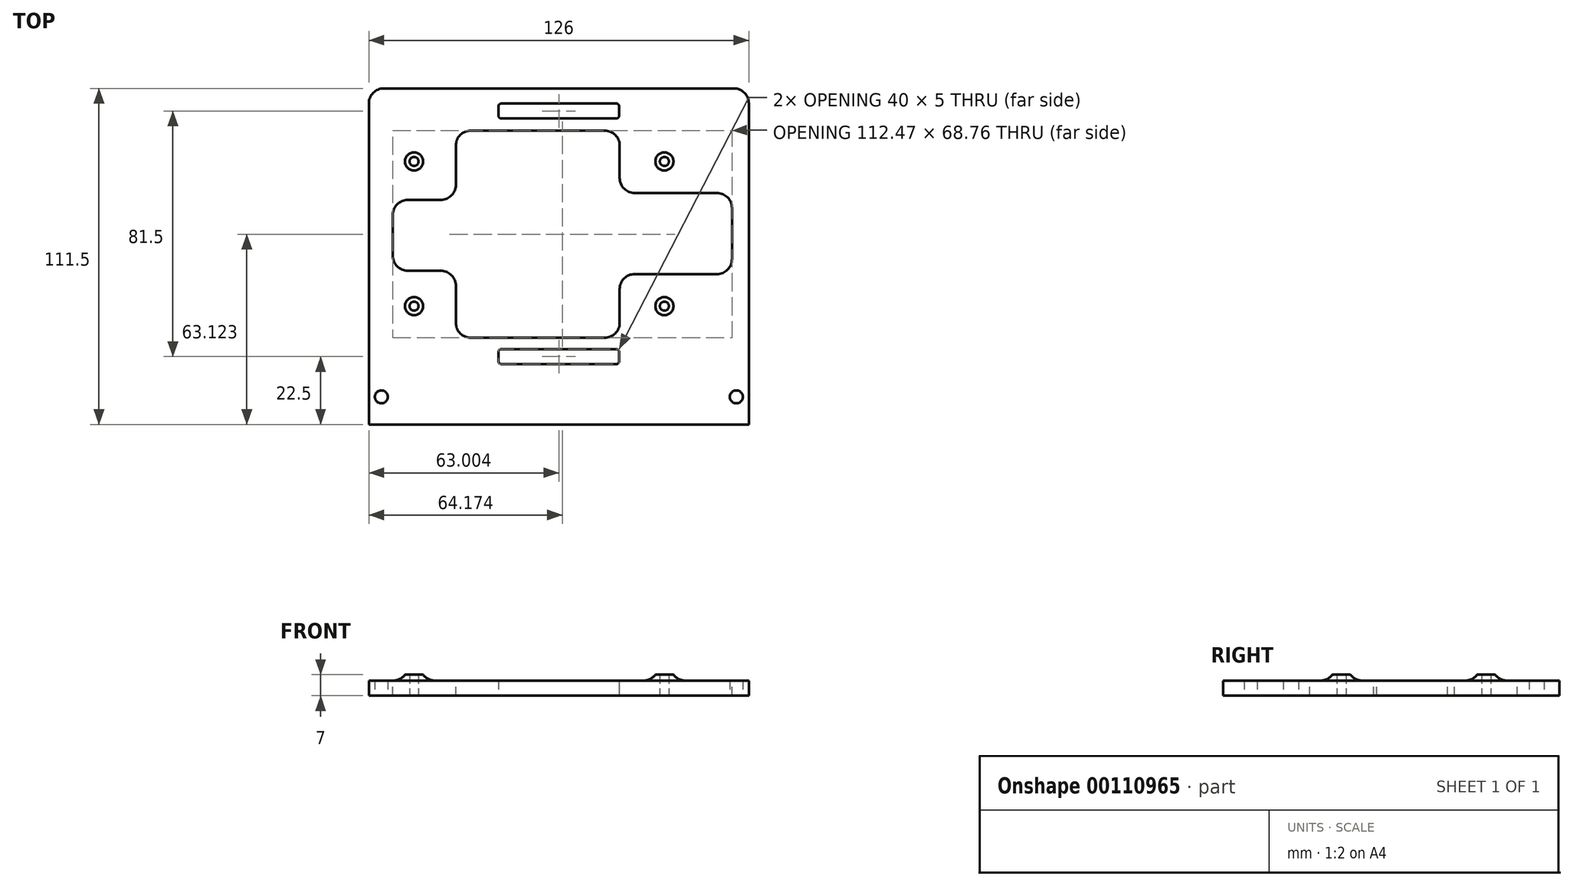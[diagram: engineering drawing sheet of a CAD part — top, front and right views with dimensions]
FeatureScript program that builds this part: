
annotation { "Feature Type Name" : "Feature", "Feature Type Description" : "" }
export const myFeature = defineFeature(function(context is Context, id is Id, definition is map)
    precondition{}
    {
        {
            var Q0;
            Q0=qCreatedBy(makeId("Top.planeOp"),FACE);
            var sketch = newSketch(context, id + "F0", { "sketchPlane" : qUnion([Q0])});
            skLineSegment(sketch, "E0.bottom", {"start": v(-49.76, 0) * mm, "end": v(76.24, 0) * mm});
            skLineSegment(sketch, "E0.top", {"start": v(-49.76, 111.5) * mm, "end": v(76.24, 111.5) * mm});
            skLineSegment(sketch, "E0.left", {"start": v(-49.76, 0) * mm, "end": v(-49.76, 111.5) * mm});
            skLineSegment(sketch, "E0.right", {"start": v(76.24, 0) * mm, "end": v(76.24, 111.5) * mm});
            skLineSegment(sketch, "E1.top", {"start": v(-49.76, 20) * mm, "end": v(76.24, 20) * mm});
            skLineSegment(sketch, "E1.left", {"start": v(-49.76, 0) * mm, "end": v(-49.76, 20) * mm});
            skLineSegment(sketch, "E1.right", {"start": v(76.24, 0) * mm, "end": v(76.24, 20) * mm});
            skLineSegment(sketch, "E2.bottom", {"start": v(-6.76, 20) * mm, "end": v(33.24, 20) * mm});
            skLineSegment(sketch, "E2.top", {"start": v(-6.76, 25) * mm, "end": v(33.24, 25) * mm});
            skLineSegment(sketch, "E2.left", {"start": v(-6.76, 20) * mm, "end": v(-6.76, 25) * mm});
            skLineSegment(sketch, "E2.right", {"start": v(33.24, 20) * mm, "end": v(33.24, 25) * mm});
            skPoint(sketch, "E3", {"position": v(13.24, 111.5) * mm});
            skPoint(sketch, "E4", {"position": v(13.24, 25) * mm});
            skLineSegment(sketch, "E5.top", {"start": v(-49.76, 106.5) * mm, "end": v(76.24, 106.5) * mm});
            skLineSegment(sketch, "E5.left", {"start": v(-49.76, 111.5) * mm, "end": v(-49.76, 106.5) * mm});
            skLineSegment(sketch, "E5.right", {"start": v(76.24, 111.5) * mm, "end": v(76.24, 106.5) * mm});
            skCircle(sketch, "E6", {"center": v(13.24, 63.25) * mm, "radius": 5 * mm});
            skCircle(sketch, "E7", {"center": v(23.24, 53.25) * mm, "radius": 1.5 * mm});
            skCircle(sketch, "E8", {"center": v(3.24, 53.25) * mm, "radius": 1.5 * mm});
            skCircle(sketch, "E9", {"center": v(3.24, 73.25) * mm, "radius": 1.5 * mm});
            skCircle(sketch, "E10", {"center": v(23.24, 73.25) * mm, "radius": 1.5 * mm});
            skLineSegment(sketch, "E11", {"start": v(23.24, 73.25) * mm, "end": v(23.24, 53.25) * mm, "construction": true});
            skLineSegment(sketch, "E12", {"start": v(3.24, 73.25) * mm, "end": v(23.24, 73.25) * mm, "construction": true});
            skPoint(sketch, "E13", {"position": v(23.24, 63.25) * mm});
            skPoint(sketch, "E14", {"position": v(13.24, 73.25) * mm});
            skLineSegment(sketch, "E15", {"start": v(23.24, 73.25) * mm, "end": v(23.24, 106.5) * mm, "construction": true});
            skLineSegment(sketch, "E16", {"start": v(23.24, 53.25) * mm, "end": v(23.24, 20) * mm, "construction": true});
            skCircle(sketch, "E17", {"center": v(-34.76, 87.25) * mm, "radius": 3 * mm});
            skCircle(sketch, "E18", {"center": v(-34.76, 39.25) * mm, "radius": 3 * mm});
            skCircle(sketch, "E19", {"center": v(48.24, 87.25) * mm, "radius": 3 * mm});
            skCircle(sketch, "E20", {"center": v(48.24, 39.25) * mm, "radius": 3 * mm});
            skLineSegment(sketch, "E21", {"start": v(-34.76, 87.25) * mm, "end": v(48.24, 87.25) * mm, "construction": true});
            skLineSegment(sketch, "E22", {"start": v(48.24, 87.25) * mm, "end": v(48.24, 39.25) * mm, "construction": true});
            skCircle(sketch, "E23", {"center": v(-34.76, 87.25) * mm, "radius": 1.5 * mm});
            skCircle(sketch, "E24", {"center": v(-34.76, 39.25) * mm, "radius": 1.5 * mm});
            skCircle(sketch, "E25", {"center": v(48.24, 39.25) * mm, "radius": 1.5 * mm});
            skCircle(sketch, "E26", {"center": v(48.24, 87.25) * mm, "radius": 1.5 * mm});
            skLineSegment(sketch, "E27", {"start": v(48.24, 39.25) * mm, "end": v(48.24, 20) * mm, "construction": true});
            skLineSegment(sketch, "E28", {"start": v(48.24, 87.25) * mm, "end": v(48.24, 106.5) * mm, "construction": true});
            skCircle(sketch, "E29", {"center": v(-45.6, 9.15) * mm, "radius": 2.15 * mm});
            skCircle(sketch, "E30", {"center": v(72.1, 9.15) * mm, "radius": 2.15 * mm});
            skLineSegment(sketch, "E31.bottom", {"start": v(-6.76, 106.5) * mm, "end": v(33.24, 106.5) * mm});
            skLineSegment(sketch, "E31.top", {"start": v(-6.76, 101.5) * mm, "end": v(33.24, 101.5) * mm});
            skLineSegment(sketch, "E31.left", {"start": v(-6.76, 106.5) * mm, "end": v(-6.76, 101.5) * mm});
            skLineSegment(sketch, "E31.right", {"start": v(33.24, 106.5) * mm, "end": v(33.24, 101.5) * mm});
            skSolve(sketch);
        }
        {
            var Q0;
            Q0=qSketchRegion(id+"F0",true);
            var Q1;
            Q1=makeQuery(id+"F0.imprint","IMPRINT",FACE,{"disambiguationData":[TD([[makeQuery(id+"F0.imprint","IMPRINT",EDGE,{"derivedFrom":sQuery(id+"F0.wireOp",EDGE,"E18")}),1.0]])]});
            var Q2;
            Q2=makeQuery(id+"F0.imprint","IMPRINT",FACE,{"disambiguationData":[TD([[makeQuery(id+"F0.imprint","IMPRINT",EDGE,{"derivedFrom":sQuery(id+"F0.wireOp",EDGE,"E17")}),1.0]])]});
            var Q3;
            Q3=makeQuery(id+"F0.imprint","IMPRINT",FACE,{"disambiguationData":[TD([[makeQuery(id+"F0.imprint","IMPRINT",EDGE,{"derivedFrom":sQuery(id+"F0.wireOp",EDGE,"E20")}),1.0]])]});
            var Q4;
            Q4=makeQuery(id+"F0.imprint","IMPRINT",FACE,{"disambiguationData":[TD([[makeQuery(id+"F0.imprint","IMPRINT",EDGE,{"derivedFrom":sQuery(id+"F0.wireOp",EDGE,"E19")}),1.0]])]});
            var Q5;
            Q5=makeQuery(id+"F0.imprint","IMPRINT",FACE,{"disambiguationData":[TD([[makeQuery(id+"F0.imprint","IMPRINT",EDGE,{"derivedFrom":sQuery(id+"F0.wireOp",EDGE,"E6")}),1.0]])]});
            var Q6;
            Q6=makeQuery(id+"F0.imprint","IMPRINT",FACE,{"disambiguationData":[TD([[makeQuery(id+"F0.imprint","IMPRINT",EDGE,{"derivedFrom":sQuery(id+"F0.wireOp",EDGE,"E9")}),1.0]])]});
            var Q7;
            Q7=makeQuery(id+"F0.imprint","IMPRINT",FACE,{"disambiguationData":[TD([[makeQuery(id+"F0.imprint","IMPRINT",EDGE,{"derivedFrom":sQuery(id+"F0.wireOp",EDGE,"E8")}),1.0]])]});
            var Q8;
            Q8=makeQuery(id+"F0.imprint","IMPRINT",FACE,{"disambiguationData":[TD([[makeQuery(id+"F0.imprint","IMPRINT",EDGE,{"derivedFrom":sQuery(id+"F0.wireOp",EDGE,"E7")}),1.0]])]});
            var Q9;
            Q9=makeQuery(id+"F0.imprint","IMPRINT",FACE,{"disambiguationData":[TD([[makeQuery(id+"F0.imprint","IMPRINT",EDGE,{"derivedFrom":sQuery(id+"F0.wireOp",EDGE,"E10")}),1.0]])]});
            extrude(context, id + "F1", {"entities" : qUnion([Q0, Q1, Q2, Q3, Q4, Q5, Q6, Q7, Q8, Q9]), "depth" : 5 * mm});
        }
        {
            var Q0;
            Q0=makeQuery(id+"F1.opExtrude","SWEPT_EDGE",EDGE,{"disambiguationData":[OSD([sQuery(id+"F0.wireOp",EDGE,"E2.top"),sQuery(id+"F0.wireOp",EDGE,"E2.left")])]});
            var Q1;
            Q1=makeQuery(id+"F1.opExtrude","SWEPT_EDGE",EDGE,{"disambiguationData":[OSD([sQuery(id+"F0.wireOp",EDGE,"E2.top"),sQuery(id+"F0.wireOp",EDGE,"E2.right")])]});
            var Q2;
            Q2=makeQuery(id+"F1.opExtrude","SWEPT_EDGE",EDGE,{"disambiguationData":[OSD([sQuery(id+"F0.wireOp",EDGE,"E1.top"),sQuery(id+"F0.wireOp",EDGE,"E2.bottom"),sQuery(id+"F0.wireOp",EDGE,"E2.left")])]});
            var Q3;
            Q3=makeQuery(id+"F1.opExtrude","SWEPT_EDGE",EDGE,{"disambiguationData":[OSD([sQuery(id+"F0.wireOp",EDGE,"E1.top"),sQuery(id+"F0.wireOp",EDGE,"E2.bottom"),sQuery(id+"F0.wireOp",EDGE,"E2.right")])]});
            var Q4;
            Q4=makeQuery(id+"F1.opExtrude","SWEPT_EDGE",EDGE,{"disambiguationData":[OSD([sQuery(id+"F0.wireOp",EDGE,"E31.top"),sQuery(id+"F0.wireOp",EDGE,"E31.left")])]});
            var Q5;
            Q5=makeQuery(id+"F1.opExtrude","SWEPT_EDGE",EDGE,{"disambiguationData":[OSD([sQuery(id+"F0.wireOp",EDGE,"E5.top"),sQuery(id+"F0.wireOp",EDGE,"E31.bottom"),sQuery(id+"F0.wireOp",EDGE,"E31.left")])]});
            var Q6;
            Q6=makeQuery(id+"F1.opExtrude","SWEPT_EDGE",EDGE,{"disambiguationData":[OSD([sQuery(id+"F0.wireOp",EDGE,"E5.top"),sQuery(id+"F0.wireOp",EDGE,"E31.bottom"),sQuery(id+"F0.wireOp",EDGE,"E31.right")])]});
            var Q7;
            Q7=makeQuery(id+"F1.opExtrude","SWEPT_EDGE",EDGE,{"disambiguationData":[OSD([sQuery(id+"F0.wireOp",EDGE,"E31.top"),sQuery(id+"F0.wireOp",EDGE,"E31.right")])]});
            fillet(context, id + "F2", {"entities" : qUnion([Q0, Q1, Q2, Q3, Q4, Q5, Q6, Q7]), "radius" : 1 * mm, "tangentPropagation" : true, "allowEdgeOverflow" : false});
        }
        {
            var Q0;
            {var subQ0=sQuery(id+"F0.wireOp",EDGE,"E5.left");var subQ1=sQuery(id+"F0.wireOp",EDGE,"E0.top");Q0=makeQuery(id+"FNY0aRx3992dt0J_1.boolean.opBoolean","MERGE",EDGE,{"derivedFrom":[makeQuery(id+"F1.opExtrude","SWEPT_EDGE",EDGE,{"disambiguationData":[OSD([subQ1,subQ0])]}),makeQuery(id+"FNY0aRx3992dt0J_1.opExtrude","SWEPT_EDGE",EDGE,{"disambiguationData":[OSD([subQ1,subQ0])]})]});}
            var Q1;
            {var subQ0=sQuery(id+"F0.wireOp",EDGE,"E1.left");var subQ1=sQuery(id+"F0.wireOp",EDGE,"E0.bottom");Q1=makeQuery(id+"FNY0aRx3992dt0J_1.boolean.opBoolean","MERGE",EDGE,{"derivedFrom":[makeQuery(id+"F1.opExtrude","SWEPT_EDGE",EDGE,{"disambiguationData":[OSD([subQ1,subQ0])]}),makeQuery(id+"FNY0aRx3992dt0J_1.opExtrude","SWEPT_EDGE",EDGE,{"disambiguationData":[OSD([subQ1,subQ0])]})]});}
            var Q2;
            Q2=makeQuery(id+"F1.opExtrude","SWEPT_EDGE",EDGE,{"disambiguationData":[OSD([sQuery(id+"F0.wireOp",EDGE,"E0.bottom"),sQuery(id+"F0.wireOp",EDGE,"E1.left")])]});
            var Q3;
            Q3=makeQuery(id+"F1.opExtrude","SWEPT_EDGE",EDGE,{"disambiguationData":[OSD([sQuery(id+"F0.wireOp",EDGE,"E0.bottom"),sQuery(id+"F0.wireOp",EDGE,"E1.right")])]});
            var Q4;
            Q4=makeQuery(id+"F1.opExtrude","SWEPT_EDGE",EDGE,{"disambiguationData":[OSD([sQuery(id+"F0.wireOp",EDGE,"E0.top"),sQuery(id+"F0.wireOp",EDGE,"E5.right")])]});
            fillet(context, id + "F3", {"entities" : qUnion([Q0, Q1, Q2, Q3, Q4]), "radius" : 5 * mm, "tangentPropagation" : true, "allowEdgeOverflow" : false});
        }
        {
            var Q0;
            Q0=makeQuery(id+"F0.imprint","IMPRINT",FACE,{"disambiguationData":[TD([[makeQuery(id+"F0.imprint","IMPRINT",EDGE,{"derivedFrom":sQuery(id+"F0.wireOp",EDGE,"E17")}),1.0]])]});
            var Q1;
            Q1=makeQuery(id+"F0.imprint","IMPRINT",FACE,{"disambiguationData":[TD([[makeQuery(id+"F0.imprint","IMPRINT",EDGE,{"derivedFrom":sQuery(id+"F0.wireOp",EDGE,"E18")}),1.0]])]});
            var Q2;
            Q2=makeQuery(id+"F0.imprint","IMPRINT",FACE,{"disambiguationData":[TD([[makeQuery(id+"F0.imprint","IMPRINT",EDGE,{"derivedFrom":sQuery(id+"F0.wireOp",EDGE,"E19")}),1.0]])]});
            var Q3;
            Q3=makeQuery(id+"F0.imprint","IMPRINT",FACE,{"disambiguationData":[TD([[makeQuery(id+"F0.imprint","IMPRINT",EDGE,{"derivedFrom":sQuery(id+"F0.wireOp",EDGE,"E20")}),1.0]])]});
            extrude(context, id + "F4", {"entities" : qUnion([Q0, Q1, Q2, Q3]), "operationType" : NewBodyOperationType.ADD, "depth" : 7 * mm});
        }
        {
            var Q0;
            Q0=makeQuery(id+"F4.boolean.opBoolean","INTERSECT",EDGE,{"derivedFrom":[makeQuery(id+"F1.opExtrude","CAP_FACE",FACE,{"disambiguationData":[OSD([sQuery(id+"F0.wireOp",EDGE,"E0.left"),sQuery(id+"F0.wireOp",EDGE,"E0.right"),sQuery(id+"F0.wireOp",EDGE,"E0.bottom"),sQuery(id+"F0.wireOp",EDGE,"E1.left"),sQuery(id+"F0.wireOp",EDGE,"E1.right"),sQuery(id+"F0.wireOp",EDGE,"E2.bottom"),sQuery(id+"F0.wireOp",EDGE,"E2.top"),sQuery(id+"F0.wireOp",EDGE,"E2.left"),sQuery(id+"F0.wireOp",EDGE,"E2.right"),sQuery(id+"F0.wireOp",EDGE,"E0.top"),sQuery(id+"F0.wireOp",EDGE,"E5.left"),sQuery(id+"F0.wireOp",EDGE,"E5.right"),sQuery(id+"F0.wireOp",EDGE,"E6"),sQuery(id+"F0.wireOp",EDGE,"E7"),sQuery(id+"F0.wireOp",EDGE,"E8"),sQuery(id+"F0.wireOp",EDGE,"E9"),sQuery(id+"F0.wireOp",EDGE,"E10")])],"isStart":false}),makeQuery(id+"F4.opExtrude","SWEPT_FACE",FACE,{"disambiguationData":[OSD([sQuery(id+"F0.wireOp",EDGE,"E17")])]})]});
            var Q1;
            Q1=makeQuery(id+"F4.boolean.opBoolean","INTERSECT",EDGE,{"derivedFrom":[makeQuery(id+"F1.opExtrude","CAP_FACE",FACE,{"disambiguationData":[OSD([sQuery(id+"F0.wireOp",EDGE,"E0.left"),sQuery(id+"F0.wireOp",EDGE,"E0.right"),sQuery(id+"F0.wireOp",EDGE,"E0.bottom"),sQuery(id+"F0.wireOp",EDGE,"E1.left"),sQuery(id+"F0.wireOp",EDGE,"E1.right"),sQuery(id+"F0.wireOp",EDGE,"E2.bottom"),sQuery(id+"F0.wireOp",EDGE,"E2.top"),sQuery(id+"F0.wireOp",EDGE,"E2.left"),sQuery(id+"F0.wireOp",EDGE,"E2.right"),sQuery(id+"F0.wireOp",EDGE,"E0.top"),sQuery(id+"F0.wireOp",EDGE,"E5.left"),sQuery(id+"F0.wireOp",EDGE,"E5.right"),sQuery(id+"F0.wireOp",EDGE,"E6"),sQuery(id+"F0.wireOp",EDGE,"E7"),sQuery(id+"F0.wireOp",EDGE,"E8"),sQuery(id+"F0.wireOp",EDGE,"E9"),sQuery(id+"F0.wireOp",EDGE,"E10")])],"isStart":false}),makeQuery(id+"F4.opExtrude","SWEPT_FACE",FACE,{"disambiguationData":[OSD([sQuery(id+"F0.wireOp",EDGE,"E18")])]})]});
            var Q2;
            Q2=makeQuery(id+"F4.boolean.opBoolean","INTERSECT",EDGE,{"derivedFrom":[makeQuery(id+"F1.opExtrude","CAP_FACE",FACE,{"disambiguationData":[OSD([sQuery(id+"F0.wireOp",EDGE,"E0.left"),sQuery(id+"F0.wireOp",EDGE,"E0.right"),sQuery(id+"F0.wireOp",EDGE,"E0.bottom"),sQuery(id+"F0.wireOp",EDGE,"E1.left"),sQuery(id+"F0.wireOp",EDGE,"E1.right"),sQuery(id+"F0.wireOp",EDGE,"E2.bottom"),sQuery(id+"F0.wireOp",EDGE,"E2.top"),sQuery(id+"F0.wireOp",EDGE,"E2.left"),sQuery(id+"F0.wireOp",EDGE,"E2.right"),sQuery(id+"F0.wireOp",EDGE,"E0.top"),sQuery(id+"F0.wireOp",EDGE,"E5.left"),sQuery(id+"F0.wireOp",EDGE,"E5.right"),sQuery(id+"F0.wireOp",EDGE,"E6"),sQuery(id+"F0.wireOp",EDGE,"E7"),sQuery(id+"F0.wireOp",EDGE,"E8"),sQuery(id+"F0.wireOp",EDGE,"E9"),sQuery(id+"F0.wireOp",EDGE,"E10")])],"isStart":false}),makeQuery(id+"F4.opExtrude","SWEPT_FACE",FACE,{"disambiguationData":[OSD([sQuery(id+"F0.wireOp",EDGE,"E20")])]})]});
            var Q3;
            Q3=makeQuery(id+"F4.boolean.opBoolean","INTERSECT",EDGE,{"derivedFrom":[makeQuery(id+"F1.opExtrude","CAP_FACE",FACE,{"disambiguationData":[OSD([sQuery(id+"F0.wireOp",EDGE,"E0.left"),sQuery(id+"F0.wireOp",EDGE,"E0.right"),sQuery(id+"F0.wireOp",EDGE,"E0.bottom"),sQuery(id+"F0.wireOp",EDGE,"E1.left"),sQuery(id+"F0.wireOp",EDGE,"E1.right"),sQuery(id+"F0.wireOp",EDGE,"E2.bottom"),sQuery(id+"F0.wireOp",EDGE,"E2.top"),sQuery(id+"F0.wireOp",EDGE,"E2.left"),sQuery(id+"F0.wireOp",EDGE,"E2.right"),sQuery(id+"F0.wireOp",EDGE,"E0.top"),sQuery(id+"F0.wireOp",EDGE,"E5.left"),sQuery(id+"F0.wireOp",EDGE,"E5.right"),sQuery(id+"F0.wireOp",EDGE,"E6"),sQuery(id+"F0.wireOp",EDGE,"E7"),sQuery(id+"F0.wireOp",EDGE,"E8"),sQuery(id+"F0.wireOp",EDGE,"E9"),sQuery(id+"F0.wireOp",EDGE,"E10")])],"isStart":false}),makeQuery(id+"F4.opExtrude","SWEPT_FACE",FACE,{"disambiguationData":[OSD([sQuery(id+"F0.wireOp",EDGE,"E19")])]})]});
            fillet(context, id + "F5", {"entities" : qUnion([Q0, Q1, Q2, Q3]), "radius" : 5 * mm, "tangentPropagation" : true, "allowEdgeOverflow" : false});
        }
        {
            var Q0;
            Q0=makeQuery(id+"F1.opExtrude","CAP_FACE",FACE,{"disambiguationData":[OSD([sQuery(id+"F0.wireOp",EDGE,"E0.left"),sQuery(id+"F0.wireOp",EDGE,"E0.right"),sQuery(id+"F0.wireOp",EDGE,"E0.bottom"),sQuery(id+"F0.wireOp",EDGE,"E1.left"),sQuery(id+"F0.wireOp",EDGE,"E1.right"),sQuery(id+"F0.wireOp",EDGE,"E2.bottom"),sQuery(id+"F0.wireOp",EDGE,"E2.top"),sQuery(id+"F0.wireOp",EDGE,"E2.left"),sQuery(id+"F0.wireOp",EDGE,"E2.right"),sQuery(id+"F0.wireOp",EDGE,"E0.top"),sQuery(id+"F0.wireOp",EDGE,"E5.left"),sQuery(id+"F0.wireOp",EDGE,"E5.right"),sQuery(id+"F0.wireOp",EDGE,"E23"),sQuery(id+"F0.wireOp",EDGE,"E24"),sQuery(id+"F0.wireOp",EDGE,"E25"),sQuery(id+"F0.wireOp",EDGE,"E26"),sQuery(id+"F0.wireOp",EDGE,"E29"),sQuery(id+"F0.wireOp",EDGE,"E30")])],"isStart":false});
            var sketch = newSketch(context, id + "F6", { "sketchPlane" : qUnion([Q0])});
            skLineSegment(sketch, "E32.bottom", {"start": v(-20.9, 97.5) * mm, "end": v(33.42, 97.5) * mm});
            skLineSegment(sketch, "E32.top", {"start": v(-20.9, 28.74) * mm, "end": v(33.42, 28.74) * mm});
            skLineSegment(sketch, "E32.left", {"start": v(-20.9, 97.5) * mm, "end": v(-20.9, 28.74) * mm});
            skLineSegment(sketch, "E32.right", {"start": v(33.42, 97.5) * mm, "end": v(33.42, 28.74) * mm});
            skLineSegment(sketch, "E33.bottom", {"start": v(-41.82, 74.5) * mm, "end": v(-20.9, 74.5) * mm});
            skLineSegment(sketch, "E33.top", {"start": v(-41.82, 50.97) * mm, "end": v(-20.9, 50.97) * mm});
            skLineSegment(sketch, "E33.left", {"start": v(-41.82, 74.5) * mm, "end": v(-41.82, 50.97) * mm});
            skLineSegment(sketch, "E33.right", {"start": v(-20.9, 74.5) * mm, "end": v(-20.9, 50.97) * mm});
            skLineSegment(sketch, "E34.bottom", {"start": v(33.42, 76.79) * mm, "end": v(70.65, 76.79) * mm});
            skLineSegment(sketch, "E34.top", {"start": v(33.42, 49.89) * mm, "end": v(70.65, 49.89) * mm});
            skLineSegment(sketch, "E34.left", {"start": v(33.42, 76.79) * mm, "end": v(33.42, 49.89) * mm});
            skLineSegment(sketch, "E34.right", {"start": v(70.65, 76.79) * mm, "end": v(70.65, 49.89) * mm});
            skSolve(sketch);
        }
        {
            var Q0;
            Q0 = qSketchRegion(id + "F6", true);
            extrude(context, id + "F7", {"entities" : qUnion([Q0]), "operationType" : NewBodyOperationType.REMOVE, "oppositeDirection" : true, "depth" : 25 * mm});
        }
        {
            var Q0;
            Q0=makeQuery(id+"F7.boolean.opBoolean","COPY",EDGE,{"derivedFrom":makeQuery(id+"F7.opExtrude","SWEPT_EDGE",EDGE,{"disambiguationData":[OSD([sQuery(id+"F6.wireOp",EDGE,"E32.left"),sQuery(id+"F6.wireOp",EDGE,"E33.bottom"),sQuery(id+"F6.wireOp",EDGE,"E33.right")])]})});
            var Q1;
            Q1=makeQuery(id+"F7.boolean.opBoolean","COPY",EDGE,{"derivedFrom":makeQuery(id+"F7.opExtrude","SWEPT_EDGE",EDGE,{"disambiguationData":[OSD([sQuery(id+"F6.wireOp",EDGE,"E32.right"),sQuery(id+"F6.wireOp",EDGE,"E34.bottom"),sQuery(id+"F6.wireOp",EDGE,"E34.left")])]})});
            var Q2;
            Q2=makeQuery(id+"F7.boolean.opBoolean","COPY",EDGE,{"derivedFrom":makeQuery(id+"F7.opExtrude","SWEPT_EDGE",EDGE,{"disambiguationData":[OSD([sQuery(id+"F6.wireOp",EDGE,"E32.right"),sQuery(id+"F6.wireOp",EDGE,"E34.top"),sQuery(id+"F6.wireOp",EDGE,"E34.left")])]})});
            var Q3;
            Q3=makeQuery(id+"F7.boolean.opBoolean","COPY",EDGE,{"derivedFrom":makeQuery(id+"F7.opExtrude","SWEPT_EDGE",EDGE,{"disambiguationData":[OSD([sQuery(id+"F6.wireOp",EDGE,"E32.left"),sQuery(id+"F6.wireOp",EDGE,"E33.top"),sQuery(id+"F6.wireOp",EDGE,"E33.right")])]})});
            var Q4;
            Q4=makeQuery(id+"F7.boolean.opBoolean","COPY",EDGE,{"derivedFrom":makeQuery(id+"F7.opExtrude","SWEPT_EDGE",EDGE,{"disambiguationData":[OSD([sQuery(id+"F6.wireOp",EDGE,"E33.top"),sQuery(id+"F6.wireOp",EDGE,"E33.left")])]})});
            var Q5;
            Q5=makeQuery(id+"F7.boolean.opBoolean","COPY",EDGE,{"derivedFrom":makeQuery(id+"F7.opExtrude","SWEPT_EDGE",EDGE,{"disambiguationData":[OSD([sQuery(id+"F6.wireOp",EDGE,"E33.bottom"),sQuery(id+"F6.wireOp",EDGE,"E33.left")])]})});
            var Q6;
            Q6=makeQuery(id+"F7.boolean.opBoolean","COPY",EDGE,{"derivedFrom":makeQuery(id+"F7.opExtrude","SWEPT_EDGE",EDGE,{"disambiguationData":[OSD([sQuery(id+"F6.wireOp",EDGE,"E32.bottom"),sQuery(id+"F6.wireOp",EDGE,"E32.left")])]})});
            var Q7;
            Q7=makeQuery(id+"F7.boolean.opBoolean","COPY",EDGE,{"derivedFrom":makeQuery(id+"F7.opExtrude","SWEPT_EDGE",EDGE,{"disambiguationData":[OSD([sQuery(id+"F6.wireOp",EDGE,"E32.bottom"),sQuery(id+"F6.wireOp",EDGE,"E32.right")])]})});
            var Q8;
            Q8=makeQuery(id+"F7.boolean.opBoolean","COPY",EDGE,{"derivedFrom":makeQuery(id+"F7.opExtrude","SWEPT_EDGE",EDGE,{"disambiguationData":[OSD([sQuery(id+"F6.wireOp",EDGE,"E34.bottom"),sQuery(id+"F6.wireOp",EDGE,"E34.right")])]})});
            var Q9;
            Q9=makeQuery(id+"F7.boolean.opBoolean","COPY",EDGE,{"derivedFrom":makeQuery(id+"F7.opExtrude","SWEPT_EDGE",EDGE,{"disambiguationData":[OSD([sQuery(id+"F6.wireOp",EDGE,"E34.top"),sQuery(id+"F6.wireOp",EDGE,"E34.right")])]})});
            var Q10;
            Q10=makeQuery(id+"F7.boolean.opBoolean","COPY",EDGE,{"derivedFrom":makeQuery(id+"F7.opExtrude","SWEPT_EDGE",EDGE,{"disambiguationData":[OSD([sQuery(id+"F6.wireOp",EDGE,"E32.top"),sQuery(id+"F6.wireOp",EDGE,"E32.right")])]})});
            var Q11;
            Q11=makeQuery(id+"F7.boolean.opBoolean","COPY",EDGE,{"derivedFrom":makeQuery(id+"F7.opExtrude","SWEPT_EDGE",EDGE,{"disambiguationData":[OSD([sQuery(id+"F6.wireOp",EDGE,"E32.top"),sQuery(id+"F6.wireOp",EDGE,"E32.left")])]})});
            fillet(context, id + "F8", {"entities" : qUnion([Q0, Q1, Q2, Q3, Q4, Q5, Q6, Q7, Q8, Q9, Q10, Q11]), "radius" : 5 * mm, "tangentPropagation" : true, "allowEdgeOverflow" : false});
        }
    });
